# Revit family: Shower-Haws_Corporation-Drench_Shower_8164
name_source: partatom
category: Plumbing Fixtures
revit_build: Autodesk Revit MEP 2013 (Build: 20130531_2115(x64)
units: mm (PartAtom-declared; Revit-internal decimal feet)

## types (1)
- Drench Shower
    Assembly Code = D2010710
    CW Connection = Yes
    CWFU = 1
    Ceiling Level = 96"
    Cost Note = For Cost information please visit the Resource tab in the Product Page URL
    Description = Outfitted with safety features like a self-regulating shower stream and universal emergency sign
    Flow = 20 GPM
    HW Connection = No
    HWFU = 1
    Keynote = 15410
    Manufacturer = Haws Corporation 1455 Kleppe Lane Sparks, NV 89431
    Model = 8164
    Product Documentation Link = http://www.hawsco.com
    Product Page URL = http://www.hawsco.com
    Pull Down Lever = 34 1/2"
    Pull Lever = Plastic - Haws Corporation - Smokey Pearl
    Series = AXION MSR™
    Shower Head = Metal - Haws Corporation - High Polished Stainless Steel - SP829
    Supply Radius = 1/2"
    Type Comments = Water is distributed at an optimal rate for the irrigation process
    URL = http://www.hawsco.com
    Vent Connection = No
    WFU = 1
    Waste Connection = Yes

## geometry (parser evidence)
native form markers: Blend x36, Sweep x8
no freeform markers — native parametric forms only
